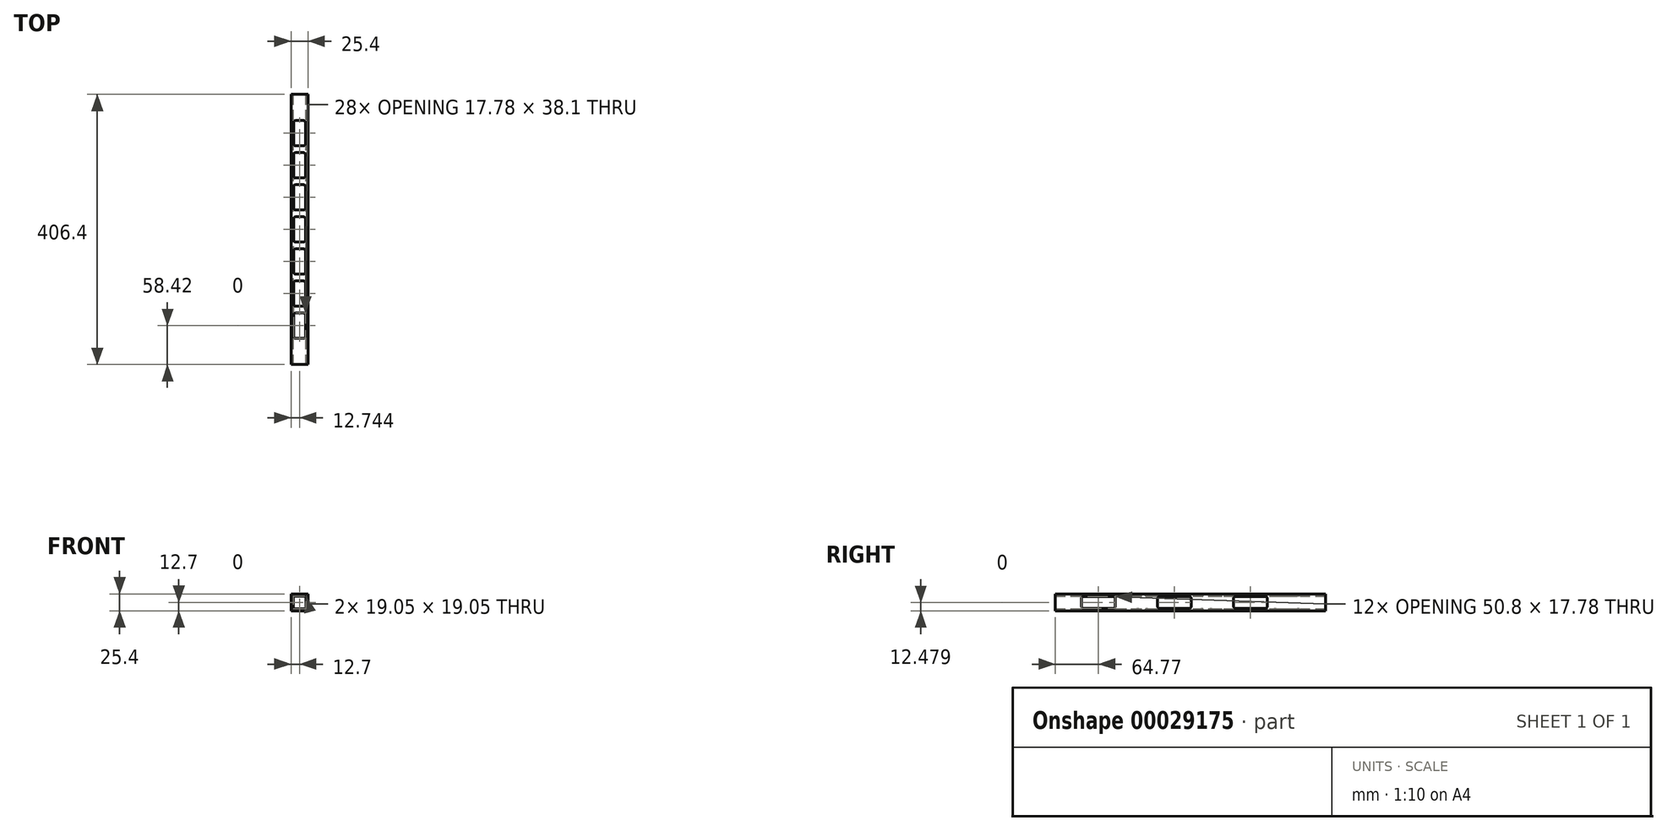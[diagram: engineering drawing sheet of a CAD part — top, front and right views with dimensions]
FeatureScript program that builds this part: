
annotation { "Feature Type Name" : "Feature", "Feature Type Description" : "" }
export const myFeature = defineFeature(function(context is Context, id is Id, definition is map)
    precondition{}
    {
        {
            var Q0;
            Q0=qCreatedBy(makeId("Front.planeOp"),FACE);
            var sketch = newSketch(context, id + "F0", { "sketchPlane" : qUnion([Q0])});
            skLineSegment(sketch, "E0.rect.bottom", {"start": v(12.7, 12.7) * mm, "end": v(-12.7, 12.7) * mm});
            skLineSegment(sketch, "E0.rect.top", {"start": v(12.7, -12.7) * mm, "end": v(-12.7, -12.7) * mm});
            skLineSegment(sketch, "E0.rect.left", {"start": v(12.7, 12.7) * mm, "end": v(12.7, -12.7) * mm});
            skLineSegment(sketch, "E0.rect.right", {"start": v(-12.7, 12.7) * mm, "end": v(-12.7, -12.7) * mm});
            skPoint(sketch, "E0.rect.middle", {"position": v(0, 0) * mm});
            skLineSegment(sketch, "E1.rect.bottom", {"start": v(9.53, 9.53) * mm, "end": v(-9.53, 9.53) * mm});
            skLineSegment(sketch, "E1.rect.top", {"start": v(9.53, -9.53) * mm, "end": v(-9.53, -9.53) * mm});
            skLineSegment(sketch, "E1.rect.left", {"start": v(9.53, 9.53) * mm, "end": v(9.53, -9.53) * mm});
            skLineSegment(sketch, "E1.rect.right", {"start": v(-9.53, 9.53) * mm, "end": v(-9.53, -9.53) * mm});
            skSolve(sketch);
        }
        {
            var Q0;
            Q0 = qSketchRegion(id + "F0", true);
            extrude(context, id + "F1", {"entities" : qUnion([Q0]), "depth" : 406.4 * mm});
        }
        {
            var Q0;
            Q0=makeQuery(id+"F1.opExtrude","SWEPT_FACE",FACE,{"disambiguationData":[OSD([sQuery(id+"F0.wireOp",EDGE,"E0.rect.left")])]});
            var sketch = newSketch(context, id + "F2", { "sketchPlane" : qUnion([Q0])});
            skLineSegment(sketch, "E2.rect.bottom", {"start": v(-319.4, 8.67) * mm, "end": v(-363.86, 8.67) * mm});
            skLineSegment(sketch, "E2.rect.top", {"start": v(-319.4, -9.11) * mm, "end": v(-363.86, -9.11) * mm});
            skLineSegment(sketch, "E2.rect.left", {"start": v(-316.23, 5.5) * mm, "end": v(-316.23, -5.94) * mm});
            skLineSegment(sketch, "E2.rect.right", {"start": v(-367.03, 5.5) * mm, "end": v(-367.03, -5.94) * mm});
            skPoint(sketch, "E2.rect.middle", {"position": v(-341.63, -0.22) * mm});
            skPoint(sketch, "E3.visualSharp", {"position": v(-316.23, 8.67) * mm});
            skArc(sketch, "E3.filletArc", {"start": v(-316.23, 5.5) * mm, "mid": v(-317.16, 7.74) * mm, "end": v(-319.4, 8.67) * mm});
            skPoint(sketch, "E4.visualSharp", {"position": v(-316.23, -9.11) * mm});
            skArc(sketch, "E4.filletArc", {"start": v(-319.4, -9.11) * mm, "mid": v(-317.16, -8.18) * mm, "end": v(-316.23, -5.94) * mm});
            skPoint(sketch, "E5.visualSharp", {"position": v(-367.03, -9.11) * mm});
            skArc(sketch, "E5.filletArc", {"start": v(-367.03, -5.94) * mm, "mid": v(-366.1, -8.18) * mm, "end": v(-363.86, -9.11) * mm});
            skPoint(sketch, "E6.visualSharp", {"position": v(-367.03, 8.67) * mm});
            skArc(sketch, "E6.filletArc", {"start": v(-363.86, 8.67) * mm, "mid": v(-366.1, 7.74) * mm, "end": v(-367.03, 5.5) * mm});
            skLineSegment(sketch, "E7.1.0.0", {"start": v(-201.93, 5.5) * mm, "end": v(-201.93, -5.94) * mm});
            skArc(sketch, "E7.1.0.1", {"start": v(-201.93, 5.5) * mm, "mid": v(-202.86, 7.74) * mm, "end": v(-205.1, 8.67) * mm});
            skLineSegment(sketch, "E7.1.0.2", {"start": v(-205.1, 8.67) * mm, "end": v(-249.56, 8.67) * mm});
            skArc(sketch, "E7.1.0.3", {"start": v(-249.56, 8.67) * mm, "mid": v(-251.8, 7.74) * mm, "end": v(-252.73, 5.5) * mm});
            skLineSegment(sketch, "E7.1.0.4", {"start": v(-252.73, 5.5) * mm, "end": v(-252.73, -5.94) * mm});
            skArc(sketch, "E7.1.0.5", {"start": v(-252.73, -5.94) * mm, "mid": v(-251.8, -8.18) * mm, "end": v(-249.56, -9.11) * mm});
            skLineSegment(sketch, "E7.1.0.6", {"start": v(-205.1, -9.11) * mm, "end": v(-249.56, -9.11) * mm});
            skLineSegment(sketch, "E7.2.0.0", {"start": v(-87.63, 5.5) * mm, "end": v(-87.63, -5.94) * mm});
            skArc(sketch, "E7.2.0.1", {"start": v(-87.63, 5.5) * mm, "mid": v(-88.56, 7.74) * mm, "end": v(-90.8, 8.67) * mm});
            skLineSegment(sketch, "E7.2.0.2", {"start": v(-90.8, 8.67) * mm, "end": v(-135.26, 8.67) * mm});
            skArc(sketch, "E7.2.0.3", {"start": v(-135.26, 8.67) * mm, "mid": v(-137.5, 7.74) * mm, "end": v(-138.43, 5.5) * mm});
            skLineSegment(sketch, "E7.2.0.4", {"start": v(-138.43, 5.5) * mm, "end": v(-138.43, -5.94) * mm});
            skArc(sketch, "E7.2.0.5", {"start": v(-138.43, -5.94) * mm, "mid": v(-137.5, -8.18) * mm, "end": v(-135.26, -9.11) * mm});
            skLineSegment(sketch, "E7.2.0.6", {"start": v(-90.8, -9.11) * mm, "end": v(-135.26, -9.11) * mm});
            skLineSegment(sketch, "E7.direction1", {"start": v(-316.23, -5.94) * mm, "end": v(-201.93, -5.94) * mm, "construction": true});
            skArc(sketch, "E8.1.0.0", {"start": v(-205.1, -9.11) * mm, "mid": v(-202.86, -8.18) * mm, "end": v(-201.93, -5.94) * mm});
            skArc(sketch, "E8.2.0.0", {"start": v(-90.8, -9.11) * mm, "mid": v(-88.56, -8.18) * mm, "end": v(-87.63, -5.94) * mm});
            skLineSegment(sketch, "E8.direction1", {"start": v(-319.4, -9.11) * mm, "end": v(-205.1, -9.11) * mm, "construction": true});
            skLineSegment(sketch, "E9", {"start": v(-406.4, 0) * mm, "end": v(-367.03, 0) * mm});
            skLineSegment(sketch, "E10", {"start": v(0, 0) * mm, "end": v(-26.67, 0) * mm});
            skSolve(sketch);
        }
        {
            var Q0;
            Q0 = qSketchRegion(id + "F2", true);
            extrude(context, id + "F3", {"entities" : qUnion([Q0]), "operationType" : NewBodyOperationType.REMOVE, "oppositeDirection" : true, "depth" : 25.4 * mm});
        }
        {
            var Q0;
            Q0=makeQuery(id+"F1.opExtrude","SWEPT_FACE",FACE,{"disambiguationData":[OSD([sQuery(id+"F0.wireOp",EDGE,"E0.rect.bottom")])]});
            var sketch = newSketch(context, id + "F4", { "sketchPlane" : qUnion([Q0])});
            skLineSegment(sketch, "E11.rect.bottom", {"start": v(5.76, -328.93) * mm, "end": v(-5.67, -328.93) * mm});
            skLineSegment(sketch, "E11.rect.top", {"start": v(5.76, -367.03) * mm, "end": v(-5.67, -367.03) * mm});
            skLineSegment(sketch, "E11.rect.left", {"start": v(8.93, -332.1) * mm, "end": v(8.93, -363.85) * mm});
            skLineSegment(sketch, "E11.rect.right", {"start": v(-8.85, -332.1) * mm, "end": v(-8.85, -363.85) * mm});
            skPoint(sketch, "E11.rect.middle", {"position": v(0.04, -347.98) * mm});
            skPoint(sketch, "E12.visualSharp", {"position": v(-8.85, -328.93) * mm});
            skArc(sketch, "E12.filletArc", {"start": v(-5.67, -328.93) * mm, "mid": v(-7.92, -329.86) * mm, "end": v(-8.85, -332.1) * mm});
            skPoint(sketch, "E13.visualSharp", {"position": v(8.93, -328.93) * mm});
            skArc(sketch, "E13.filletArc", {"start": v(8.93, -332.1) * mm, "mid": v(8, -329.86) * mm, "end": v(5.76, -328.93) * mm});
            skPoint(sketch, "E14.visualSharp", {"position": v(8.93, -367.03) * mm});
            skArc(sketch, "E14.filletArc", {"start": v(5.76, -367.03) * mm, "mid": v(8, -366.1) * mm, "end": v(8.93, -363.85) * mm});
            skPoint(sketch, "E15.visualSharp", {"position": v(-8.85, -367.03) * mm});
            skArc(sketch, "E15.filletArc", {"start": v(-8.85, -363.85) * mm, "mid": v(-7.92, -366.1) * mm, "end": v(-5.67, -367.03) * mm});
            skLineSegment(sketch, "E16.0.1.0", {"start": v(5.76, -280.67) * mm, "end": v(-5.67, -280.67) * mm});
            skArc(sketch, "E16.0.1.1", {"start": v(-5.67, -280.67) * mm, "mid": v(-7.92, -281.6) * mm, "end": v(-8.85, -283.84) * mm});
            skLineSegment(sketch, "E16.0.1.2", {"start": v(-8.85, -283.84) * mm, "end": v(-8.85, -315.6) * mm});
            skArc(sketch, "E16.0.1.3", {"start": v(-8.85, -315.6) * mm, "mid": v(-7.92, -317.84) * mm, "end": v(-5.67, -318.77) * mm});
            skLineSegment(sketch, "E16.0.1.4", {"start": v(5.76, -318.77) * mm, "end": v(-5.67, -318.77) * mm});
            skArc(sketch, "E16.0.1.5", {"start": v(5.76, -318.77) * mm, "mid": v(8, -317.84) * mm, "end": v(8.93, -315.6) * mm});
            skLineSegment(sketch, "E16.0.1.6", {"start": v(8.93, -283.84) * mm, "end": v(8.93, -315.6) * mm});
            skArc(sketch, "E16.0.1.7", {"start": v(8.93, -283.84) * mm, "mid": v(8, -281.6) * mm, "end": v(5.76, -280.67) * mm});
            skLineSegment(sketch, "E16.0.2.0", {"start": v(5.76, -232.4) * mm, "end": v(-5.67, -232.4) * mm});
            skArc(sketch, "E16.0.2.1", {"start": v(-5.67, -232.4) * mm, "mid": v(-7.92, -233.34) * mm, "end": v(-8.85, -235.58) * mm});
            skLineSegment(sketch, "E16.0.2.2", {"start": v(-8.85, -235.58) * mm, "end": v(-8.85, -267.33) * mm});
            skArc(sketch, "E16.0.2.3", {"start": v(-8.85, -267.33) * mm, "mid": v(-7.92, -269.58) * mm, "end": v(-5.67, -270.5) * mm});
            skLineSegment(sketch, "E16.0.2.4", {"start": v(5.76, -270.5) * mm, "end": v(-5.67, -270.5) * mm});
            skArc(sketch, "E16.0.2.5", {"start": v(5.76, -270.5) * mm, "mid": v(8, -269.58) * mm, "end": v(8.93, -267.33) * mm});
            skLineSegment(sketch, "E16.0.2.6", {"start": v(8.93, -235.58) * mm, "end": v(8.93, -267.33) * mm});
            skArc(sketch, "E16.0.2.7", {"start": v(8.93, -235.58) * mm, "mid": v(8, -233.34) * mm, "end": v(5.76, -232.4) * mm});
            skLineSegment(sketch, "E16.0.3.0", {"start": v(5.76, -184.15) * mm, "end": v(-5.67, -184.15) * mm});
            skArc(sketch, "E16.0.3.1", {"start": v(-5.67, -184.15) * mm, "mid": v(-7.92, -185.08) * mm, "end": v(-8.85, -187.32) * mm});
            skLineSegment(sketch, "E16.0.3.2", {"start": v(-8.85, -187.32) * mm, "end": v(-8.85, -219.07) * mm});
            skArc(sketch, "E16.0.3.3", {"start": v(-8.85, -219.07) * mm, "mid": v(-7.92, -221.32) * mm, "end": v(-5.67, -222.25) * mm});
            skLineSegment(sketch, "E16.0.3.4", {"start": v(5.76, -222.25) * mm, "end": v(-5.67, -222.25) * mm});
            skArc(sketch, "E16.0.3.5", {"start": v(5.76, -222.25) * mm, "mid": v(8, -221.32) * mm, "end": v(8.93, -219.07) * mm});
            skLineSegment(sketch, "E16.0.3.6", {"start": v(8.93, -187.32) * mm, "end": v(8.93, -219.07) * mm});
            skArc(sketch, "E16.0.3.7", {"start": v(8.93, -187.32) * mm, "mid": v(8, -185.08) * mm, "end": v(5.76, -184.15) * mm});
            skLineSegment(sketch, "E16.0.4.0", {"start": v(5.76, -135.89) * mm, "end": v(-5.67, -135.89) * mm});
            skArc(sketch, "E16.0.4.1", {"start": v(-5.67, -135.89) * mm, "mid": v(-7.92, -136.82) * mm, "end": v(-8.85, -139.06) * mm});
            skLineSegment(sketch, "E16.0.4.2", {"start": v(-8.85, -139.06) * mm, "end": v(-8.85, -170.81) * mm});
            skArc(sketch, "E16.0.4.3", {"start": v(-8.85, -170.81) * mm, "mid": v(-7.92, -173.06) * mm, "end": v(-5.67, -173.99) * mm});
            skLineSegment(sketch, "E16.0.4.4", {"start": v(5.76, -173.99) * mm, "end": v(-5.67, -173.99) * mm});
            skArc(sketch, "E16.0.4.5", {"start": v(5.76, -173.99) * mm, "mid": v(8, -173.06) * mm, "end": v(8.93, -170.81) * mm});
            skLineSegment(sketch, "E16.0.4.6", {"start": v(8.93, -139.06) * mm, "end": v(8.93, -170.81) * mm});
            skArc(sketch, "E16.0.4.7", {"start": v(8.93, -139.06) * mm, "mid": v(8, -136.82) * mm, "end": v(5.76, -135.89) * mm});
            skLineSegment(sketch, "E16.0.5.0", {"start": v(5.76, -87.63) * mm, "end": v(-5.67, -87.63) * mm});
            skArc(sketch, "E16.0.5.1", {"start": v(-5.67, -87.63) * mm, "mid": v(-7.92, -88.56) * mm, "end": v(-8.85, -90.8) * mm});
            skLineSegment(sketch, "E16.0.5.2", {"start": v(-8.85, -90.8) * mm, "end": v(-8.85, -122.55) * mm});
            skArc(sketch, "E16.0.5.3", {"start": v(-8.85, -122.55) * mm, "mid": v(-7.92, -124.8) * mm, "end": v(-5.67, -125.73) * mm});
            skLineSegment(sketch, "E16.0.5.4", {"start": v(5.76, -125.73) * mm, "end": v(-5.67, -125.73) * mm});
            skArc(sketch, "E16.0.5.5", {"start": v(5.76, -125.73) * mm, "mid": v(8, -124.8) * mm, "end": v(8.93, -122.55) * mm});
            skLineSegment(sketch, "E16.0.5.6", {"start": v(8.93, -90.8) * mm, "end": v(8.93, -122.55) * mm});
            skArc(sketch, "E16.0.5.7", {"start": v(8.93, -90.8) * mm, "mid": v(8, -88.56) * mm, "end": v(5.76, -87.63) * mm});
            skLineSegment(sketch, "E16.0.6.0", {"start": v(5.76, -39.37) * mm, "end": v(-5.67, -39.37) * mm});
            skArc(sketch, "E16.0.6.1", {"start": v(-5.67, -39.37) * mm, "mid": v(-7.92, -40.3) * mm, "end": v(-8.85, -42.55) * mm});
            skLineSegment(sketch, "E16.0.6.2", {"start": v(-8.85, -42.55) * mm, "end": v(-8.85, -74.3) * mm});
            skArc(sketch, "E16.0.6.3", {"start": v(-8.85, -74.3) * mm, "mid": v(-7.92, -76.54) * mm, "end": v(-5.67, -77.47) * mm});
            skLineSegment(sketch, "E16.0.6.4", {"start": v(5.76, -77.47) * mm, "end": v(-5.67, -77.47) * mm});
            skArc(sketch, "E16.0.6.5", {"start": v(5.76, -77.47) * mm, "mid": v(8, -76.54) * mm, "end": v(8.93, -74.3) * mm});
            skLineSegment(sketch, "E16.0.6.6", {"start": v(8.93, -42.55) * mm, "end": v(8.93, -74.3) * mm});
            skArc(sketch, "E16.0.6.7", {"start": v(8.93, -42.55) * mm, "mid": v(8, -40.3) * mm, "end": v(5.76, -39.37) * mm});
            skLineSegment(sketch, "E16.direction1", {"start": v(-5.67, -328.93) * mm, "end": v(18.66, -328.93) * mm, "construction": true});
            skLineSegment(sketch, "E16.direction2", {"start": v(-5.67, -328.93) * mm, "end": v(-5.67, -280.67) * mm, "construction": true});
            skSolve(sketch);
        }
        {
            var Q0;
            Q0 = qSketchRegion(id + "F4", true);
            extrude(context, id + "F5", {"entities" : qUnion([Q0]), "operationType" : NewBodyOperationType.REMOVE, "oppositeDirection" : true, "depth" : 25.4 * mm});
        }
    });
